# Revit family: E_Ceiling Junction Box_MEPcontent_Spelsberg_U 71 DAD_INT-EN
name_source: partatom
category: Electrical Fixtures
revit_build: Autodesk Revit 2017 (Build: 20160225_1515(x64)
units: mm (PartAtom-declared; Revit-internal decimal feet)

## family parameters
Always vertical = No
Cut with Voids When Loaded = No
Maintain Annotation Orientation = Yes
OmniClass Number = 23.80.30.14.24
OmniClass Title = Junction Boxes
Part Type = Junction Box
Room Calculation Point = No
Round Connector Dimension = Use Diameter
Shared = No
Work Plane-Based = No

## types (1)
- U 71 DAD
    3D Representation = 3DGeometry
    Angle = 0.00°
    Article Description = Ceiling luminaire junction box U 71 DAD
    Article Type = U 71 DAD
    Conduit Diameter 1 = 20 mm
    Conduit Diameter 2 = 25 mm  [stored 0.082021 ft]
    Description = Ceiling luminaire junction box U 71 DAD
    ETIM Article Class = EC002601
    Height = 86 mm
    IFCExportAs = IfcJunctionBox
    IFCExportType = NOTDEFINED
    Length = 71 mm  [stored 0.23294 ft]
    Manufacturer = Spelsberg
    Manufacturer Art. No. = 97154801
    Manufacturer URL = http://www.spelsberg.com
    Model = U 71 DAD
    Placeholder Height = 47 mm
    Product Line = Spelsberg
    Revit Version = 2017
    Rotation U-Axis Correction = 0.00°
    Rotation U-Axis Default Correction = 0.00°
    Rotation V-Axis Correction = 0.00°
    Rotation V-Axis Default Correction = 0.00°
    Rotation W-Axis Correction = 0.00°
    Rotation W-Axis Default Correction = 0.00°
    Voltage = 230 V
    Width = 71 mm  [stored 0.23294 ft]

note: [stored X ft] marks values corroborated as IEEE doubles in the binary element streams (Revit-internal decimal feet)

## geometry (parser evidence)
native form markers: Sweep x24
no freeform markers — native parametric forms only
